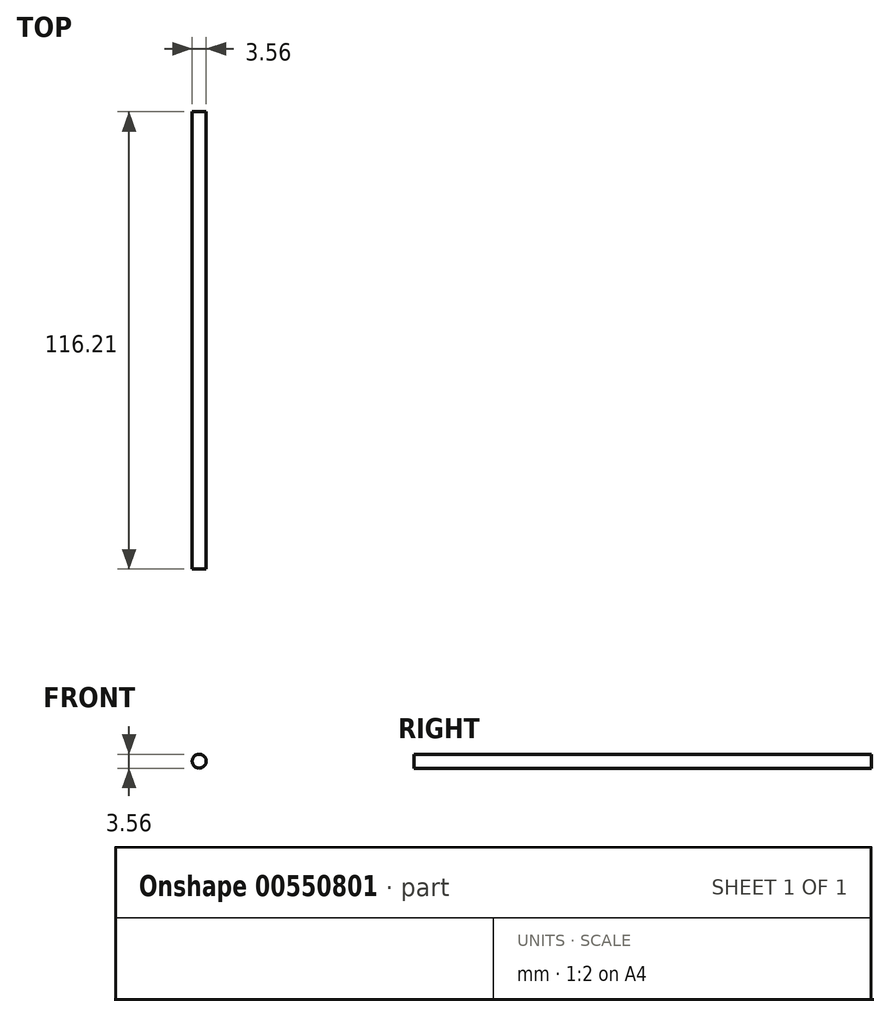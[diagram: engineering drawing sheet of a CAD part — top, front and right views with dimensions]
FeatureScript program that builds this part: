
annotation { "Feature Type Name" : "Feature", "Feature Type Description" : "" }
export const myFeature = defineFeature(function(context is Context, id is Id, definition is map)
    precondition{}
    {
        {
            var Q0;
            Q0=qCreatedBy(makeId("Front.planeOp"),FACE);
            var sketch = newSketch(context, id + "F0", { "sketchPlane" : qUnion([Q0])});
            skCircle(sketch, "E0", {"center": v(0, 0) * mm, "radius": 1.78 * mm});
            skSolve(sketch);
        }
        {
            var Q0;
            Q0=makeQuery(id+"F0.imprint","IMPRINT",FACE,{"disambiguationData":[TD([[makeQuery(id+"F0.imprint","IMPRINT",EDGE,{"derivedFrom":sQuery(id+"F0.wireOp",EDGE,"E0")}),1.0]])]});
            extrude(context, id + "F1", {"entities" : qUnion([Q0]), "depth" : 116.2 * mm, "offsetDistance" : 25.4 * mm});
        }
    });
